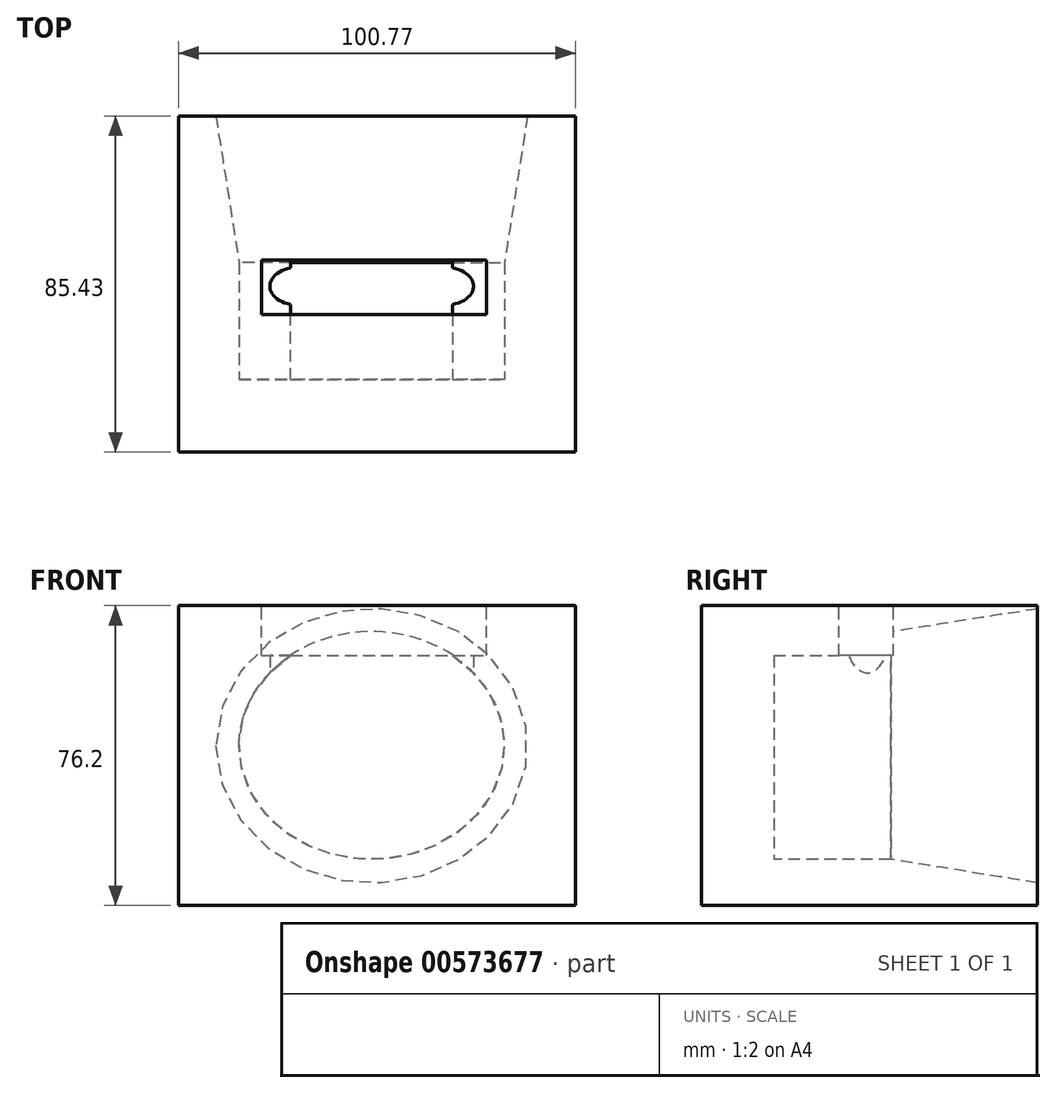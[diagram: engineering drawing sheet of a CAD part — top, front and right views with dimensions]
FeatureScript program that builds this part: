
annotation { "Feature Type Name" : "Feature", "Feature Type Description" : "" }
export const myFeature = defineFeature(function(context is Context, id is Id, definition is map)
    precondition{}
    {
        {
            var Q0;
            Q0=qCreatedBy(makeId("Top.planeOp"),FACE);
            var sketch = newSketch(context, id + "F0", { "sketchPlane" : qUnion([Q0])});
            skLineSegment(sketch, "E0.bottom", {"start": v(-49.03, 37.3) * mm, "end": v(51.74, 37.3) * mm});
            skLineSegment(sketch, "E0.top", {"start": v(-49.03, -48.13) * mm, "end": v(51.74, -48.13) * mm});
            skLineSegment(sketch, "E0.left", {"start": v(-49.03, 37.3) * mm, "end": v(-49.03, -48.13) * mm});
            skLineSegment(sketch, "E0.right", {"start": v(51.74, 37.3) * mm, "end": v(51.74, -48.13) * mm});
            skSolve(sketch);
        }
        {
            var Q0;
            Q0=makeQuery(id+"F0.imprint","IMPRINT",FACE,{"disambiguationData":[TD([[makeQuery(id+"F0.imprint","IMPRINT",EDGE,{"derivedFrom":sQuery(id+"F0.wireOp",EDGE,"E0.bottom")}),-1.0]])]});
            extrude(context, id + "F1", {"entities" : qUnion([Q0]), "depth" : 76.2 * mm, "offsetDistance" : 25.4 * mm});
        }
        {
            var Q0;
            Q0=makeQuery(id+"F1.opExtrude","CAP_FACE",FACE,{"disambiguationData":[OSD([sQuery(id+"F0.wireOp",EDGE,"E0.bottom"),sQuery(id+"F0.wireOp",EDGE,"E0.top"),sQuery(id+"F0.wireOp",EDGE,"E0.left"),sQuery(id+"F0.wireOp",EDGE,"E0.right")])],"isStart":false});
            var sketch = newSketch(context, id + "F2", { "sketchPlane" : qUnion([Q0])});
            skLineSegment(sketch, "E1", {"start": v(-27.97, 0.7) * mm, "end": v(-27.97, -12.63) * mm});
            skLineSegment(sketch, "E2", {"start": v(-27.97, -12.63) * mm, "end": v(29.18, -12.63) * mm});
            skLineSegment(sketch, "E3", {"start": v(-27.97, 0.7) * mm, "end": v(29.18, 0.7) * mm});
            skLineSegment(sketch, "E4", {"start": v(29.18, 0.7) * mm, "end": v(29.18, -12.63) * mm});
            skSolve(sketch);
        }
        {
            var Q0;
            Q0=makeQuery(id+"F2.imprint","IMPRINT",FACE,{"disambiguationData":[TD([[makeQuery(id+"F2.imprint","IMPRINT",EDGE,{"derivedFrom":sQuery(id+"F2.wireOp",EDGE,"E1")}),1.0]])]});
            extrude(context, id + "F3", {"entities" : qUnion([Q0]), "operationType" : NewBodyOperationType.REMOVE, "oppositeDirection" : true, "depth" : 12.7 * mm, "offsetDistance" : 25.4 * mm});
        }
        {
            var Q0;
            Q0=makeQuery(id+"F3.boolean.opBoolean","COPY",FACE,{"derivedFrom":makeQuery(id+"F3.opExtrude","CAP_FACE",FACE,{"disambiguationData":[OSD([sQuery(id+"F2.wireOp",EDGE,"E1"),sQuery(id+"F2.wireOp",EDGE,"E2"),sQuery(id+"F2.wireOp",EDGE,"E3"),sQuery(id+"F2.wireOp",EDGE,"E4")])],"isStart":false})});
            var sketch = newSketch(context, id + "F4", { "sketchPlane" : qUnion([Q0])});
            skEllipse(sketch, "E5", {"center": v(-18.35, -5.97) * mm, "majorRadius": 7.52 * mm, "minorRadius": 4.86 * mm, "majorAxis": v(1, 0)});
            skPoint(sketch, "E5.centerSnap0", {"position": v(-27.97, -5.97) * mm});
            skEllipse(sketch, "E6.MirrorC", {"center": v(18.35, -5.97) * mm, "majorRadius": 7.52 * mm, "minorRadius": 4.86 * mm, "majorAxis": v(-1, 0)});
            skSolve(sketch);
        }
        {
            var Q0;
            Q0=makeQuery(id+"F4.imprint","IMPRINT",FACE,{"disambiguationData":[TD([[makeQuery(id+"F4.imprint","IMPRINT",EDGE,{"derivedFrom":sQuery(id+"F4.wireOp",EDGE,"E5")}),1.0]])]});
            var Q1;
            Q1=makeQuery(id+"F4.imprint","IMPRINT",FACE,{"disambiguationData":[TD([[makeQuery(id+"F4.imprint","IMPRINT",EDGE,{"derivedFrom":sQuery(id+"F4.wireOp",EDGE,"E6.MirrorC")}),1.0]])]});
            extrude(context, id + "F5", {"entities" : qUnion([Q0, Q1]), "operationType" : NewBodyOperationType.REMOVE, "oppositeDirection" : true, "depth" : 39.12 * mm, "offsetDistance" : 25.4 * mm});
        }
        {
            var Q0;
            Q0=qCreatedBy(makeId("Front.planeOp"),FACE);
            var sketch = newSketch(context, id + "F6", { "sketchPlane" : qUnion([Q0])});
            skEllipse(sketch, "E7", {"center": v(0, 40.6) * mm, "majorRadius": 33.69 * mm, "minorRadius": 28.9 * mm, "majorAxis": v(-1, 0)});
            skSolve(sketch);
        }
        {
            var Q0;
            Q0=makeQuery(id+"F6.imprint","IMPRINT",FACE,{"disambiguationData":[TD([[makeQuery(id+"F6.imprint","IMPRINT",EDGE,{"derivedFrom":sQuery(id+"F6.wireOp",EDGE,"E7")}),1.0]])]});
            extrude(context, id + "F7", {"entities" : qUnion([Q0]), "operationType" : NewBodyOperationType.REMOVE, "oppositeDirection" : true, "depth" : 50.8 * mm, "offsetDistance" : 25.4 * mm, "hasDraft" : true, "draftAngle" : 9 * degree});
        }
        {
            var Q0;
            Q0=makeQuery(id+"F7.boolean.opBoolean","COPY",FACE,{"derivedFrom":makeQuery(id+"F7.opExtrude","CAP_FACE",FACE,{"disambiguationData":[OSD([sQuery(id+"F6.wireOp",EDGE,"E7")])],"isStart":true})});
            var Q1;
            Q1=makeQuery(id+"F3.boolean.opBoolean","COPY",FACE,{"derivedFrom":makeQuery(id+"F3.opExtrude","SWEPT_FACE",FACE,{"disambiguationData":[OSD([sQuery(id+"F2.wireOp",EDGE,"E2")])]})});
            extrude(context, id + "F8", {"entities" : qUnion([Q0, Q1]), "operationType" : NewBodyOperationType.REMOVE, "oppositeDirection" : true, "depth" : 29.72 * mm, "offsetDistance" : 25.4 * mm});
        }
        {
            var Q0;
            Q0=makeQuery(id+"F8.boolean.opBoolean","COPY",FACE,{"derivedFrom":makeQuery(id+"F8.opExtrude","CAP_FACE",FACE,{"disambiguationData":[OSD([sQuery(id+"F2.wireOp",EDGE,"E2")])],"isStart":false})});
            extrude(context, id + "F9", {"entities" : qUnion([Q0]), "operationType" : NewBodyOperationType.ADD, "depth" : 29.2 * mm, "offsetDistance" : 25.4 * mm});
        }
    });
